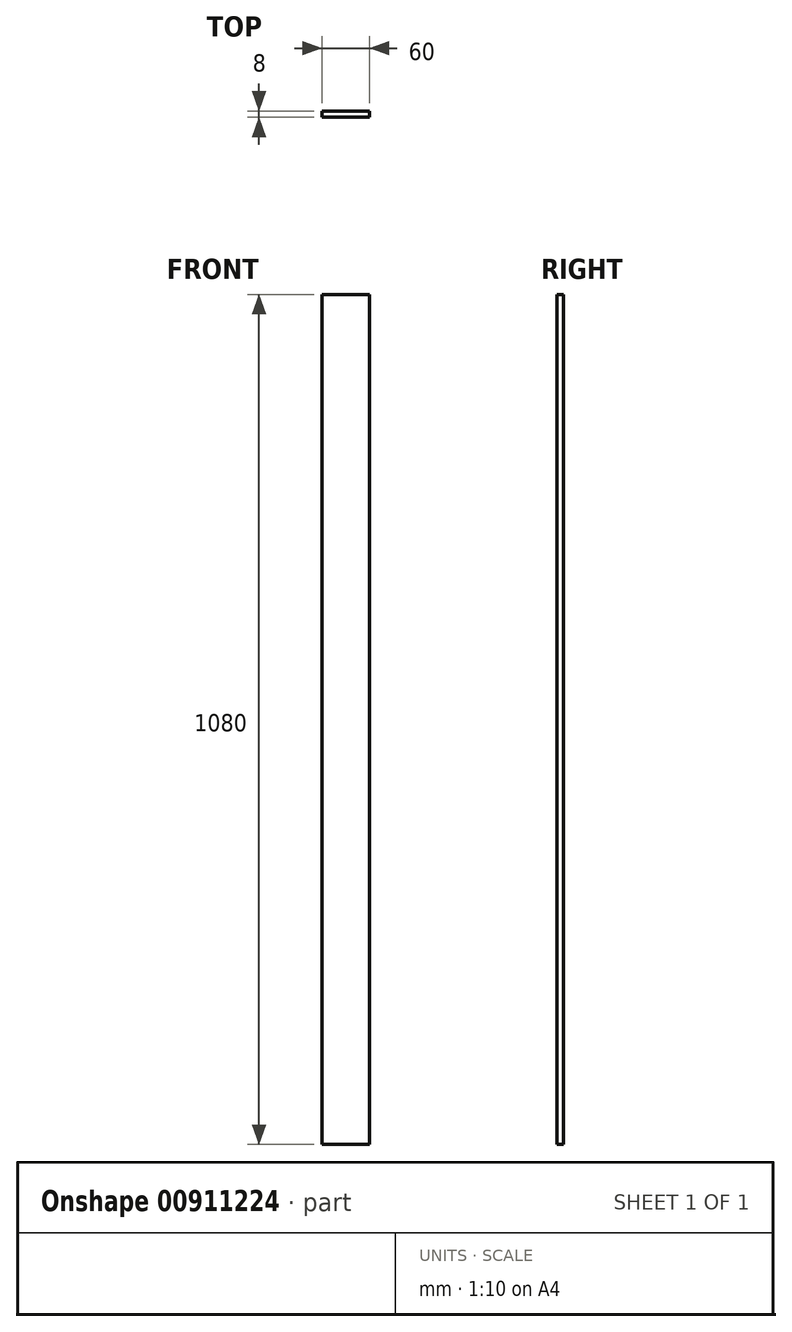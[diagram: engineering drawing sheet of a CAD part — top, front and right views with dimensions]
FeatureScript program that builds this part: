
annotation { "Feature Type Name" : "Feature", "Feature Type Description" : "" }
export const myFeature = defineFeature(function(context is Context, id is Id, definition is map)
    precondition{}
    {
        {
            var Q0;
            Q0=qCreatedBy(makeId("Front.planeOp"),FACE);
            var sketch = newSketch(context, id + "F0", { "sketchPlane" : qUnion([Q0])});
            skLineSegment(sketch, "E0.bottom", {"start": v(30, 540) * mm, "end": v(-30, 540) * mm});
            skLineSegment(sketch, "E0.top", {"start": v(30, -540) * mm, "end": v(-30, -540) * mm});
            skLineSegment(sketch, "E0.left", {"start": v(30, 540) * mm, "end": v(30, -540) * mm});
            skLineSegment(sketch, "E0.right", {"start": v(-30, 540) * mm, "end": v(-30, -540) * mm});
            skPoint(sketch, "E0.middle", {"position": v(0, 0) * mm});
            skSolve(sketch);
        }
        {
            var Q0;
            Q0=makeQuery(id+"F0.imprint","IMPRINT",FACE,{"disambiguationData":[TD([[makeQuery(id+"F0.imprint","IMPRINT",EDGE,{"derivedFrom":sQuery(id+"F0.wireOp",EDGE,"E0.bottom")}),1.0]])]});
            extrude(context, id + "F1", {"entities" : qUnion([Q0]), "depth" : 8 * mm, "offsetDistance" : 25 * mm});
        }
    });
